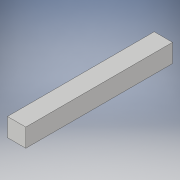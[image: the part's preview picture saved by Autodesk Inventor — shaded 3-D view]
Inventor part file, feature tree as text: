
AUTODESK INVENTOR PART (.ipt)
format: ipt  version: 2017 (Build 210142000, 142)  size: 90,624 bytes
history: native  units: in
note: dims shown in document units (in); Inventor stores cm internally (conversion verified against a paired STEP export)
features: extrude x1, sketch x1
ambient origin geometry x8: Origin, YZ Plane, XZ Plane, XY Plane, X Axis, Y Axis, Z Axis, Center Point
bodies: Solid1 (feature_tree)
feature tree (2):
  extrude  "Extrusion1"  Depth=16.0in
  sketch  "Sketch1"  dims[d0=2.0in d1=16.0in d2=2.0in d3=0.0in]
